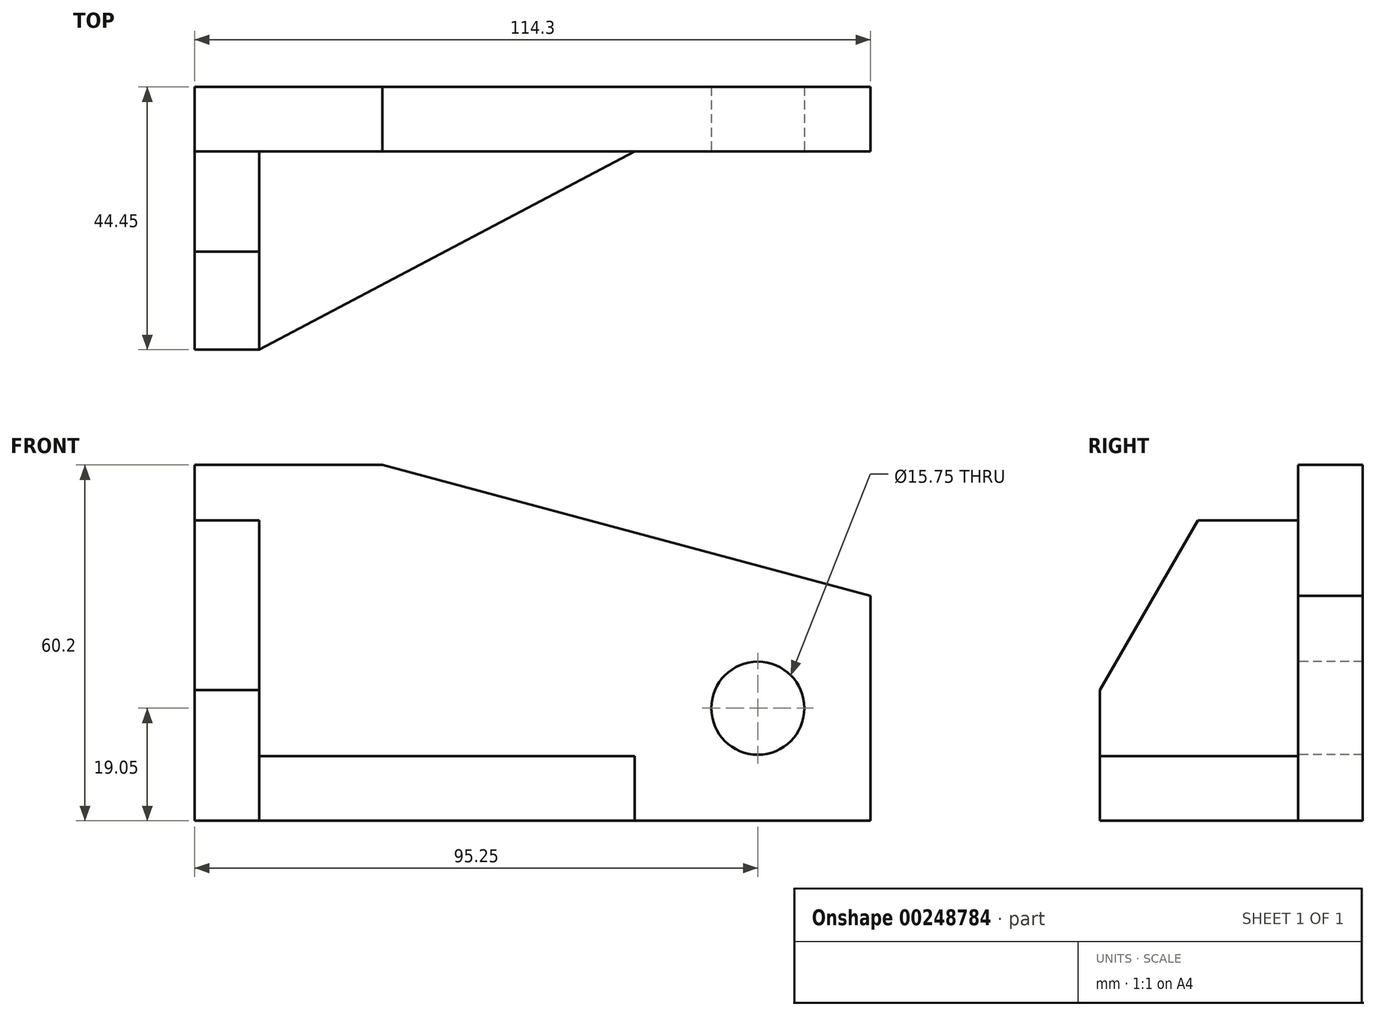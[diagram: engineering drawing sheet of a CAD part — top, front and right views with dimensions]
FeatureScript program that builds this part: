
annotation { "Feature Type Name" : "Feature", "Feature Type Description" : "" }
export const myFeature = defineFeature(function(context is Context, id is Id, definition is map)
    precondition{}
    {
        {
            var Q0;
            Q0=qCreatedBy(makeId("Front.planeOp"),FACE);
            var sketch = newSketch(context, id + "F0", { "sketchPlane" : qUnion([Q0])});
            skLineSegment(sketch, "E0.bottom", {"start": v(0, 0) * mm, "end": v(114.3, 0) * mm});
            skLineSegment(sketch, "E0.top", {"start": v(0, 60.2) * mm, "end": v(31.75, 60.2) * mm});
            skLineSegment(sketch, "E0.left", {"start": v(0, 0) * mm, "end": v(0, 60.2) * mm});
            skLineSegment(sketch, "E1", {"start": v(0, 50.8) * mm, "end": v(10.92, 50.8) * mm});
            skLineSegment(sketch, "E2", {"start": v(10.92, 50.8) * mm, "end": v(10.92, 0) * mm});
            skLineSegment(sketch, "E3", {"start": v(31.75, 60.2) * mm, "end": v(114.3, 38.08) * mm});
            skLineSegment(sketch, "E4", {"start": v(31.75, 60.2) * mm, "end": v(108.65, 60.2) * mm, "construction": true});
            skLineSegment(sketch, "E5", {"start": v(114.3, 0) * mm, "end": v(114.3, 38.08) * mm});
            skLineSegment(sketch, "E6", {"start": v(10.92, 10.92) * mm, "end": v(74.42, 10.92) * mm});
            skLineSegment(sketch, "E7", {"start": v(74.42, 10.92) * mm, "end": v(74.42, 0) * mm});
            skLineSegment(sketch, "E8", {"start": v(95.25, 0) * mm, "end": v(95.25, 19.05) * mm, "construction": true});
            skLineSegment(sketch, "E9", {"start": v(95.25, 19.05) * mm, "end": v(114.3, 19.05) * mm, "construction": true});
            skCircle(sketch, "E10", {"center": v(95.25, 19.05) * mm, "radius": 7.87 * mm});
            skSolve(sketch);
        }
        {
            var Q0;
            {var subQ5=sQuery(id+"F0.wireOp",EDGE,"E0.top");Q0=makeQuery(id+"F0.imprint","IMPRINT",FACE,{"disambiguationData":[TD([[makeQuery(id+"F0.imprint","IMPRINT",EDGE,{"derivedFrom":subQ5}),-1.0]])]});}
            var Q1;
            {var subQ0=sQuery(id+"F0.wireOp",EDGE,"E6");Q1=makeQuery(id+"F0.imprint","IMPRINT",FACE,{"disambiguationData":[TD([[makeQuery(id+"F0.imprint","IMPRINT",EDGE,{"derivedFrom":subQ0}),-1.0]])]});}
            var Q2;
            {var subQ1=sQuery(id+"F0.wireOp",EDGE,"E1");Q2=makeQuery(id+"F0.imprint","IMPRINT",FACE,{"disambiguationData":[TD([[makeQuery(id+"F0.imprint","IMPRINT",EDGE,{"derivedFrom":subQ1}),-1.0]])]});}
            extrude(context, id + "F1", {"entities" : qUnion([Q0, Q1, Q2]), "oppositeDirection" : true, "depth" : 10.92 * mm});
        }
        {
            var Q0;
            Q0=qCreatedBy(makeId("Right.planeOp"),FACE);
            var sketch = newSketch(context, id + "F2", { "sketchPlane" : qUnion([Q0])});
            skLineSegment(sketch, "E11", {"start": v(0, 50.8) * mm, "end": v(-16.96, 50.8) * mm});
            skLineSegment(sketch, "E12", {"start": v(-16.96, 50.8) * mm, "end": v(-33.53, 22.1) * mm});
            skLineSegment(sketch, "E13", {"start": v(-33.53, 22.1) * mm, "end": v(-33.53, 0) * mm});
            skLineSegment(sketch, "E14", {"start": v(-33.53, 0) * mm, "end": v(0, 0) * mm});
            skLineSegment(sketch, "E15", {"start": v(-33.53, 0) * mm, "end": v(-33.53, 50.8) * mm, "construction": true});
            skLineSegment(sketch, "E16", {"start": v(-33.53, 50.8) * mm, "end": v(0, 50.8) * mm, "construction": true});
            skLineSegment(sketch, "E17", {"start": v(0, 50.8) * mm, "end": v(0, 0) * mm});
            skSolve(sketch);
        }
        {
            var Q0;
            Q0 = qSketchRegion(id + "F2", true);
            extrude(context, id + "F3", {"entities" : qUnion([Q0]), "depth" : 10.92 * mm});
        }
        {
            var Q0;
            Q0=qCreatedBy(makeId("Top.planeOp"),FACE);
            var sketch = newSketch(context, id + "F4", { "sketchPlane" : qUnion([Q0])});
            skLineSegment(sketch, "E18", {"start": v(0, -33.53) * mm, "end": v(10.92, -33.53) * mm});
            skLineSegment(sketch, "E19", {"start": v(10.92, -33.53) * mm, "end": v(10.92, 0) * mm});
            skLineSegment(sketch, "E20", {"start": v(10.92, 0) * mm, "end": v(0, 0) * mm});
            skLineSegment(sketch, "E21", {"start": v(0, -33.53) * mm, "end": v(0, 0) * mm});
            skLineSegment(sketch, "E22", {"start": v(10.92, 0) * mm, "end": v(74.42, 0) * mm});
            skLineSegment(sketch, "E23", {"start": v(74.42, 0) * mm, "end": v(10.92, -33.53) * mm});
            skSolve(sketch);
        }
        {
            var Q0;
            Q0=makeQuery(id+"F4.imprint","IMPRINT",FACE,{"disambiguationData":[TD([[makeQuery(id+"F4.imprint","IMPRINT",EDGE,{"derivedFrom":sQuery(id+"F4.wireOp",EDGE,"E19")}),-1.0]])]});
            extrude(context, id + "F5", {"entities" : qUnion([Q0]), "depth" : 10.92 * mm});
        }
    });
